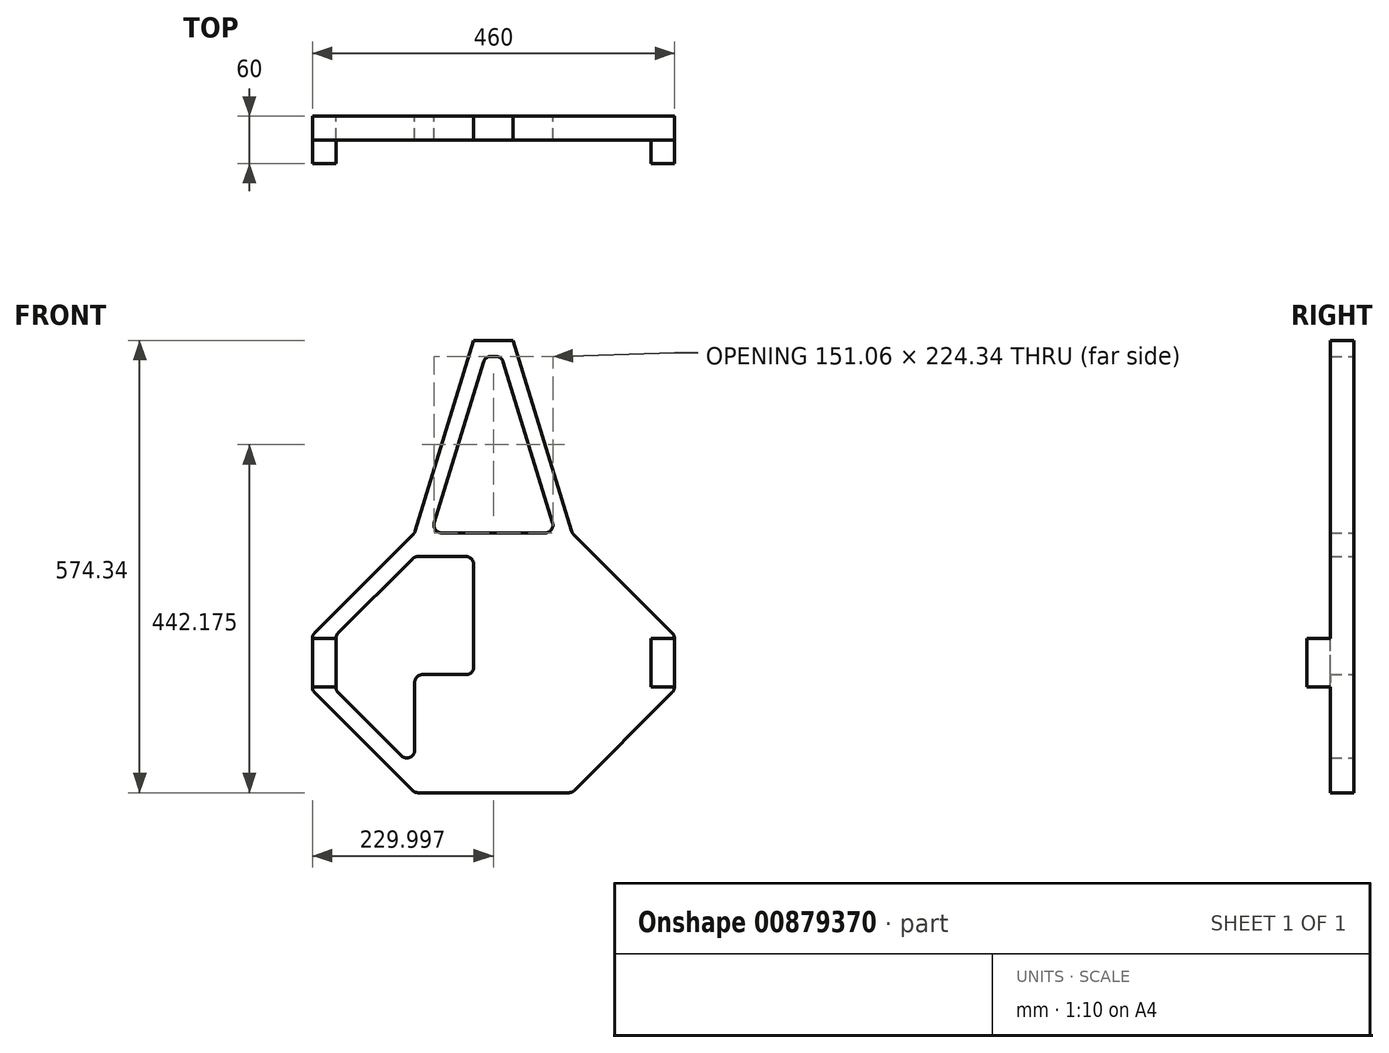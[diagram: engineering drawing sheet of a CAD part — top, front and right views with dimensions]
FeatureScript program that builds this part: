
annotation { "Feature Type Name" : "Feature", "Feature Type Description" : "" }
export const myFeature = defineFeature(function(context is Context, id is Id, definition is map)
    precondition{}
    {
        {
            var Q0;
            Q0=qCreatedBy(makeId("Front.planeOp"),FACE);
            var sketch = newSketch(context, id + "F0", { "sketchPlane" : qUnion([Q0])});
            skLineSegment(sketch, "E0", {"start": v(-168.3, -201.93) * mm, "end": v(-168.3, -116.08) * mm});
            skLineSegment(sketch, "E1", {"start": v(-158.3, -106.08) * mm, "end": v(-103.3, -106.08) * mm});
            skLineSegment(sketch, "E2", {"start": v(31.7, -116.08) * mm, "end": v(31.7, -201.93) * mm});
            skLineSegment(sketch, "E3", {"start": v(27.56, -256.08) * mm, "end": v(-164.16, -256.08) * mm});
            skLineSegment(sketch, "E4", {"start": v(-298.3, -121.93) * mm, "end": v(-298.3, -60.22) * mm});
            skLineSegment(sketch, "E5", {"start": v(131.7, -121.93) * mm, "end": v(131.7, -60.22) * mm});
            skLineSegment(sketch, "E6", {"start": v(-268.3, -121.93) * mm, "end": v(-268.3, -60.22) * mm});
            skLineSegment(sketch, "E7", {"start": v(161.7, -60.22) * mm, "end": v(161.7, -121.93) * mm});
            skLineSegment(sketch, "E8", {"start": v(158.77, -129) * mm, "end": v(34.63, -253.15) * mm});
            skLineSegment(sketch, "E9", {"start": v(-171.23, -253.15) * mm, "end": v(-295.37, -129) * mm});
            skLineSegment(sketch, "E10", {"start": v(-295.37, -53.15) * mm, "end": v(-170.06, 72.17) * mm});
            skLineSegment(sketch, "E11", {"start": v(-133.85, 73.92) * mm, "end": v(-2.75, 73.92) * mm});
            skLineSegment(sketch, "E12", {"start": v(33.46, 72.17) * mm, "end": v(158.77, -53.15) * mm});
            skLineSegment(sketch, "E13", {"start": v(128.77, -53.15) * mm, "end": v(34.63, 41) * mm});
            skLineSegment(sketch, "E14", {"start": v(27.56, 43.92) * mm, "end": v(-33.3, 43.92) * mm});
            skLineSegment(sketch, "E15", {"start": v(-171.23, 41) * mm, "end": v(-265.37, -53.15) * mm});
            skLineSegment(sketch, "E16", {"start": v(-93.3, -96.08) * mm, "end": v(-93.3, 33.92) * mm});
            skPoint(sketch, "E16.endSnap0", {"position": v(-68.3, 43.92) * mm});
            skLineSegment(sketch, "E17", {"start": v(-43.3, 33.92) * mm, "end": v(-43.3, -96.08) * mm});
            skLineSegment(sketch, "E18", {"start": v(128.77, -129) * mm, "end": v(48.77, -209) * mm});
            skLineSegment(sketch, "E19", {"start": v(-265.37, -129) * mm, "end": v(-185.37, -209) * mm});
            skLineSegment(sketch, "E20", {"start": v(-167.57, 76.3) * mm, "end": v(-93.3, 318.26) * mm});
            skLineSegment(sketch, "E21", {"start": v(-93.3, 318.26) * mm, "end": v(-43.3, 318.26) * mm});
            skLineSegment(sketch, "E22", {"start": v(-43.3, 318.26) * mm, "end": v(30.97, 76.3) * mm});
            skLineSegment(sketch, "E23.0", {"start": v(-55.92, 291.2) * mm, "end": v(6.8, 86.86) * mm});
            skLineSegment(sketch, "E23.1", {"start": v(-71.13, 298.26) * mm, "end": v(-65.48, 298.26) * mm});
            skLineSegment(sketch, "E23.2", {"start": v(-143.41, 86.86) * mm, "end": v(-80.69, 291.2) * mm});
            skLineSegment(sketch, "E24.trimOffspring", {"start": v(-103.3, 43.92) * mm, "end": v(-164.16, 43.92) * mm});
            skLineSegment(sketch, "E25.trimOffspring", {"start": v(-33.3, -106.08) * mm, "end": v(21.7, -106.08) * mm});
            skLineSegment(sketch, "E26", {"start": v(-298.3, -56.08) * mm, "end": v(-297.4, -56.08) * mm});
            skLineSegment(sketch, "E27", {"start": v(-297.4, -126.08) * mm, "end": v(-298.3, -126.08) * mm});
            skLineSegment(sketch, "E28", {"start": v(160.8, -126.08) * mm, "end": v(161.7, -126.08) * mm});
            skLineSegment(sketch, "E29", {"start": v(161.7, -56.08) * mm, "end": v(160.8, -56.08) * mm});
            skPoint(sketch, "E30.visualSharp", {"position": v(-168.3, -106.08) * mm});
            skArc(sketch, "E30.filletArc", {"start": v(-158.3, -106.08) * mm, "mid": v(-165.37, -109) * mm, "end": v(-168.3, -116.08) * mm});
            skPoint(sketch, "E31.visualSharp", {"position": v(31.7, -106.08) * mm});
            skArc(sketch, "E31.filletArc", {"start": v(31.7, -116.08) * mm, "mid": v(28.77, -109) * mm, "end": v(21.7, -106.08) * mm});
            skPoint(sketch, "E32.visualSharp", {"position": v(-168.3, -226.08) * mm});
            skArc(sketch, "E32.filletArc", {"start": v(-185.37, -209) * mm, "mid": v(-174.48, -211.17) * mm, "end": v(-168.3, -201.93) * mm});
            skPoint(sketch, "E33.visualSharp", {"position": v(31.7, -226.08) * mm});
            skArc(sketch, "E33.filletArc", {"start": v(31.7, -201.93) * mm, "mid": v(37.87, -211.17) * mm, "end": v(48.77, -209) * mm});
            skPoint(sketch, "E34.visualSharp", {"position": v(131.7, -126.08) * mm});
            skArc(sketch, "E34.filletArc", {"start": v(128.77, -129) * mm, "mid": v(130.94, -125.76) * mm, "end": v(131.7, -121.93) * mm});
            skPoint(sketch, "E35.visualSharp", {"position": v(131.7, -56.08) * mm});
            skPoint(sketch, "E36.visualSharp", {"position": v(161.7, -56.08) * mm});
            skArc(sketch, "E36.filletArc", {"start": v(161.7, -60.22) * mm, "mid": v(160.94, -56.4) * mm, "end": v(158.77, -53.15) * mm});
            skPoint(sketch, "E37.visualSharp", {"position": v(161.7, -126.08) * mm});
            skArc(sketch, "E37.filletArc", {"start": v(158.77, -129) * mm, "mid": v(160.94, -125.76) * mm, "end": v(161.7, -121.93) * mm});
            skPoint(sketch, "E38.visualSharp", {"position": v(31.7, 43.92) * mm});
            skArc(sketch, "E38.filletArc", {"start": v(34.63, 41) * mm, "mid": v(31.38, 43.16) * mm, "end": v(27.56, 43.92) * mm});
            skPoint(sketch, "E39.visualSharp", {"position": v(-43.3, 43.92) * mm});
            skArc(sketch, "E39.filletArc", {"start": v(-33.3, 43.92) * mm, "mid": v(-40.37, 41) * mm, "end": v(-43.3, 33.92) * mm});
            skPoint(sketch, "E40.visualSharp", {"position": v(-43.3, -106.08) * mm});
            skArc(sketch, "E40.filletArc", {"start": v(-43.3, -96.08) * mm, "mid": v(-40.37, -103.15) * mm, "end": v(-33.3, -106.08) * mm});
            skPoint(sketch, "E41.visualSharp", {"position": v(-93.3, -106.08) * mm});
            skArc(sketch, "E41.filletArc", {"start": v(-103.3, -106.08) * mm, "mid": v(-96.23, -103.15) * mm, "end": v(-93.3, -96.08) * mm});
            skPoint(sketch, "E42.visualSharp", {"position": v(-93.3, 43.92) * mm});
            skArc(sketch, "E42.filletArc", {"start": v(-93.3, 33.92) * mm, "mid": v(-96.23, 41) * mm, "end": v(-103.3, 43.92) * mm});
            skPoint(sketch, "E43.visualSharp", {"position": v(-168.3, 43.92) * mm});
            skArc(sketch, "E43.filletArc", {"start": v(-164.16, 43.92) * mm, "mid": v(-167.99, 43.16) * mm, "end": v(-171.23, 41) * mm});
            skPoint(sketch, "E44.visualSharp", {"position": v(-147.38, 73.92) * mm});
            skArc(sketch, "E44.filletArc", {"start": v(-143.41, 86.86) * mm, "mid": v(-141.9, 77.98) * mm, "end": v(-133.85, 73.92) * mm});
            skPoint(sketch, "E45.visualSharp", {"position": v(10.78, 73.92) * mm});
            skArc(sketch, "E45.filletArc", {"start": v(-2.75, 73.92) * mm, "mid": v(5.29, 77.98) * mm, "end": v(6.8, 86.86) * mm});
            skPoint(sketch, "E46.visualSharp", {"position": v(31.7, 73.92) * mm});
            skArc(sketch, "E46.filletArc", {"start": v(30.97, 76.3) * mm, "mid": v(31.96, 74.08) * mm, "end": v(33.46, 72.17) * mm});
            skPoint(sketch, "E47.visualSharp", {"position": v(-168.3, 73.92) * mm});
            skArc(sketch, "E47.filletArc", {"start": v(-170.06, 72.17) * mm, "mid": v(-168.56, 74.08) * mm, "end": v(-167.57, 76.3) * mm});
            skPoint(sketch, "E48.visualSharp", {"position": v(-298.3, -126.08) * mm});
            skArc(sketch, "E48.filletArc", {"start": v(-298.3, -121.93) * mm, "mid": v(-297.54, -125.76) * mm, "end": v(-295.37, -129) * mm});
            skPoint(sketch, "E49.visualSharp", {"position": v(-298.3, -56.08) * mm});
            skArc(sketch, "E49.filletArc", {"start": v(-295.37, -53.15) * mm, "mid": v(-297.54, -56.4) * mm, "end": v(-298.3, -60.22) * mm});
            skPoint(sketch, "E50.visualSharp", {"position": v(-268.3, -56.08) * mm});
            skArc(sketch, "E50.filletArc", {"start": v(-265.37, -53.15) * mm, "mid": v(-267.54, -56.4) * mm, "end": v(-268.3, -60.22) * mm});
            skPoint(sketch, "E51.visualSharp", {"position": v(-268.3, -126.08) * mm});
            skArc(sketch, "E51.filletArc", {"start": v(-268.3, -121.93) * mm, "mid": v(-267.54, -125.76) * mm, "end": v(-265.37, -129) * mm});
            skPoint(sketch, "E52.visualSharp", {"position": v(-168.3, -256.08) * mm});
            skArc(sketch, "E52.filletArc", {"start": v(-171.23, -253.15) * mm, "mid": v(-167.99, -255.31) * mm, "end": v(-164.16, -256.08) * mm});
            skPoint(sketch, "E53.visualSharp", {"position": v(31.7, -256.08) * mm});
            skArc(sketch, "E53.filletArc", {"start": v(27.56, -256.08) * mm, "mid": v(31.38, -255.31) * mm, "end": v(34.63, -253.15) * mm});
            skPoint(sketch, "E54.visualSharp", {"position": v(-58.08, 298.26) * mm});
            skArc(sketch, "E54.filletArc", {"start": v(-55.92, 291.2) * mm, "mid": v(-59.53, 296.3) * mm, "end": v(-65.48, 298.26) * mm});
            skPoint(sketch, "E55.visualSharp", {"position": v(-78.52, 298.26) * mm});
            skArc(sketch, "E55.filletArc", {"start": v(-71.13, 298.26) * mm, "mid": v(-77.07, 296.3) * mm, "end": v(-80.69, 291.2) * mm});
            skLineSegment(sketch, "E56", {"start": v(-298.3, -121.93) * mm, "end": v(-268.3, -121.93) * mm});
            skLineSegment(sketch, "E57", {"start": v(-298.3, -60.22) * mm, "end": v(-268.3, -60.22) * mm});
            skLineSegment(sketch, "E58", {"start": v(131.7, -60.22) * mm, "end": v(161.7, -60.22) * mm});
            skLineSegment(sketch, "E59", {"start": v(131.7, -121.93) * mm, "end": v(161.7, -121.93) * mm});
            skSolve(sketch);
        }
        {
            var Q0;
            Q0=makeQuery(id+"F0.imprint","IMPRINT",FACE,{"disambiguationData":[TD([[makeQuery(id+"F0.imprint","IMPRINT",EDGE,{"derivedFrom":sQuery(id+"F0.wireOp",EDGE,"E0")}),-1.0]])]});
            extrude(context, id + "F1", {"entities" : qUnion([Q0]), "depth" : 30 * mm, "offsetDistance" : 25 * mm});
        }
        {
            var Q0;
            Q0=makeQuery(id+"F0.imprint","IMPRINT",FACE,{"disambiguationData":[TD([[makeQuery(id+"F0.imprint","IMPRINT",EDGE,{"derivedFrom":sQuery(id+"F0.wireOp",EDGE,"E4")}),-1.0]])]});
            var Q1;
            Q1=makeQuery(id+"F0.imprint","IMPRINT",FACE,{"disambiguationData":[TD([[makeQuery(id+"F0.imprint","IMPRINT",EDGE,{"derivedFrom":sQuery(id+"F0.wireOp",EDGE,"E5")}),-1.0]])]});
            extrude(context, id + "F2", {"entities" : qUnion([Q0, Q1]), "operationType" : NewBodyOperationType.ADD, "depth" : 60 * mm, "offsetDistance" : 25 * mm});
        }
    });
